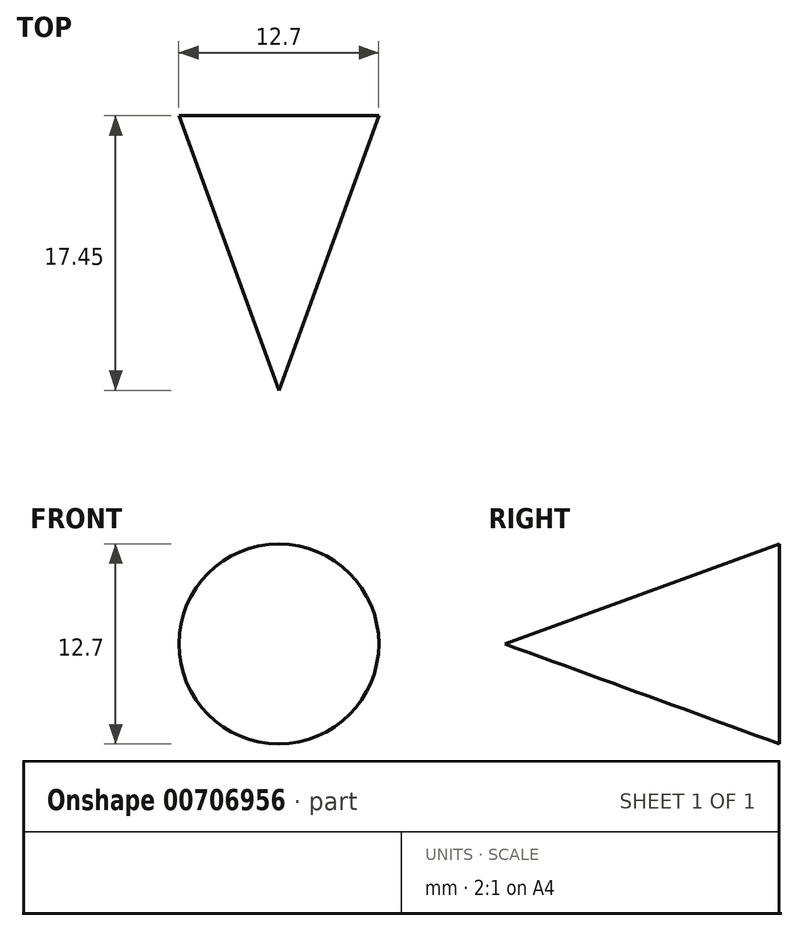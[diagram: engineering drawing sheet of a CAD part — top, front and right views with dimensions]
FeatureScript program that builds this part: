
annotation { "Feature Type Name" : "Feature", "Feature Type Description" : "" }
export const myFeature = defineFeature(function(context is Context, id is Id, definition is map)
    precondition{}
    {
        {
            var Q0;
            Q0=qCreatedBy(makeId("Front.planeOp"),FACE);
            var sketch = newSketch(context, id + "F0", { "sketchPlane" : qUnion([Q0])});
            skCircle(sketch, "E0", {"center": v(-43.28, 21.27) * mm, "radius": 6.35 * mm});
            skSolve(sketch);
        }
        {
            var Q0;
            Q0=makeQuery(id+"F0.imprint","IMPRINT",FACE,{"disambiguationData":[TD([[makeQuery(id+"F0.imprint","IMPRINT",EDGE,{"derivedFrom":sQuery(id+"F0.wireOp",EDGE,"E0")}),1.0]])]});
            extrude(context, id + "F1", {"entities" : qUnion([Q0]), "depth" : 381 * mm, "offsetDistance" : 25.4 * mm, "hasDraft" : true, "draftAngle" : 20 * degree, "draftPullDirection" : true});
        }
    });
